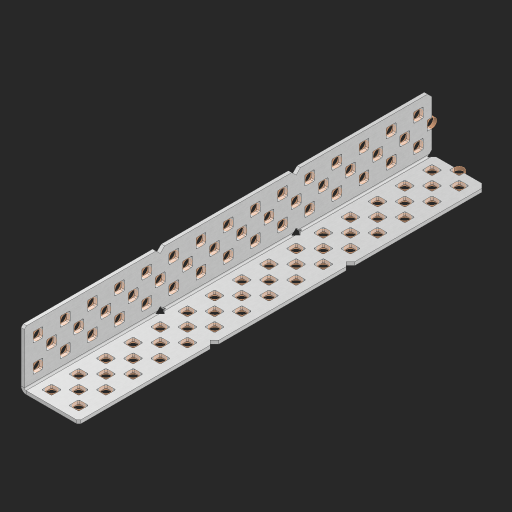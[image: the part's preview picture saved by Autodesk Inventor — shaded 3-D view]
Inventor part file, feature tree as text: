
AUTODESK INVENTOR PART (.ipt)
format: ipt  version: 2023 (Build 270158000, 158)  size: 1,245,696 bytes
history: native  units: in
note: dims shown in document units (in); Inventor stores cm internally (conversion verified against a paired STEP export)
features: other x96, extrude x88, sheet_metal_op x8, sketch x7, pattern_linear x2, mirror x1, chamfer x1
ambient origin geometry x8: Origin, YZ Plane, XZ Plane, XY Plane, X Axis, Y Axis, Z Axis, Center Point
bodies: Solid1 (feature_tree), Body (feature_tree)
feature tree (203):
  sheet_metal_op  "Flanges"
  sheet_metal_op  "Body Pattern"
  pattern_linear  "Center Pattern"  Spacing1=1.0in  [1 undecoded]
  other  "Arc Length"
  pattern_linear  "Notch Pattern"  Spacing1=0.25in  [1 undecoded]
  other  "Diagonal Plane"
  mirror  "Everything Mirrored"
  chamfer  "End Chamfer"
  sketch  "Sketch1"  dims[d0=1.0in]
  other  "Plate1"
  sketch  "Sketch2"  dims[d1=7.5in]
  other  "Plate2"
  sheet_metal_op  "Bend1"
  sheet_metal_op  "Corner1"
  sketch  "Sketch8"  dims[d2=0.0625in]
  sketch  "Sketch9"  dims[d3=0.0625in]
  other  "Srf91"
  sheet_metal_op  "Body Pattern Sketch"
  other  "Srf92"
  sketch  "Sketch13"  dims[d4=0.0312in]
  sketch  "Sketch15"  dims[d5=0.125in]
  sketch  "Sketch16"  dims[d6=0.0625in d7=1.0in d8=90.0deg d9=0.0312in d10=0.25in d11=0.0625in d12=0.0625in d49=0.182in d50=0.02in d52=0.25in d53=0.0625in d54=0.0in d55=0.172in d56=1.0in d57=0.0in d60=5.9055in d62=0.5in d63=0.7874in d65=0.5in d85=0.1473in d86=0.1782in d89=0.0625in d90=0.0in d91=0.04in d92=0.0491in d95=2.5in d96=0.04in d97=0.25in d98=45.0deg d99=0.25in d106=0.182in d107=0.02in d108=0.5in d110=0.0625in d111=0.0in d112=0.172in d113=0.5in d114=0.0in d117=0.5in d123=0.25in d125=0.25in d126=0.0491in d127=0.1473in d128=0.08in d129=0.04in d130=2.5in]
  other  "Srf786"
  other  "Srf856"
  other  "Srf857"
  other  "Srf858"
  other  "Srf859"
  other  "Srf860"
  other  "Srf861"
  other  "Srf889"
  other  "Srf890"
  other  "Srf891"
  other  "Srf1275"
  other  "Srf1276"
  other  "Srf1278"
  other  "Srf1279"
  other  "Srf1280"
  other  "Srf1281"
  other  "Srf1282"
  other  "Srf1283"
  other  "Srf1277"
  other  "Srf1285"
  other  "Srf1286"
  other  "Srf1287"
  other  "Srf1383"
  other  "Srf1384"
  other  "Srf1385"
  other  "Srf1386"
  other  "Srf1387"
  other  "Srf1388"
  other  "Srf1389"
  other  "Srf1390"
  other  "Srf1391"
  other  "Srf1392"
  other  "Srf1393"
  other  "Srf1394"
  other  "Srf1395"
  other  "Srf1396"
  other  "Srf1397"
  other  "Srf1398"
  other  "Srf1399"
  other  "Srf1400"
  other  "Srf1401"
  other  "Srf1402"
  other  "Srf1403"
  other  "Srf1404"
  other  "Srf1445"
  other  "Srf1446"
  other  "Srf1447"
  other  "Srf1448"
  other  "Srf1449"
  other  "Srf1450"
  other  "Srf1451"
  other  "Srf1452"
  other  "Srf1453"
  other  "Srf1454"
  other  "Srf1455"
  other  "Srf1475"
  other  "Srf1476"
  other  "Srf1477"
  other  "Srf1478"
  other  "Srf1479"
  other  "Srf1480"
  other  "Srf1481"
  other  "Srf1482"
  other  "Srf1483"
  other  "Srf1484"
  other  "Srf1485"
  other  "Srf1486"
  other  "Srf1487"
  other  "Srf1488"
  other  "Srf1489"
  other  "Srf1490"
  other  "Srf1491"
  other  "Srf1492"
  other  "Srf1493"
  other  "Srf1494"
  other  "Srf1495"
  other  "Srf1496"
  other  "Srf1537"
  other  "Srf1538"
  other  "Srf1539"
  other  "Srf1540"
  other  "Srf1541"
  other  "Srf1542"
  other  "Srf1543"
  other  "Srf1544"
  other  "Srf1545"
  other  "Srf1546"
  other  "Srf1547"
  sheet_metal_op  "Body Stamp"
  sheet_metal_op  "Body Circle"
  other  "Center Stamp"
  other  "Center Circle"
  sheet_metal_op  "Notch"
  extrude  "ExtrusionSrf92"  Depth=0.0625in
  extrude  "ExtrusionSrf856"  Depth=0.0625in
  extrude  "ExtrusionSrf857"  Depth=2.5in
  extrude  "ExtrusionSrf858"  Depth=2.5in
  extrude  "ExtrusionSrf859"  Depth=2.5in
  extrude  "ExtrusionSrf860"  Depth=0.0625in
  extrude  "ExtrusionSrf861"  TaperAngle=0.0deg  [1 undecoded]
  extrude  "ExtrusionSrf889"  Depth=2.5in
  extrude  "ExtrusionSrf890"  Depth=1.0in TaperAngle=0.0deg
  extrude  "ExtrusionSrf891"  Depth=2.5in
  extrude  "ExtrusionSrf1275"  Depth=0.5in
  extrude  "ExtrusionSrf1276"  Depth=2.5in
  extrude  "ExtrusionSrf1277"  Depth=2.5in
  extrude  "ExtrusionSrf1278"  Depth=0.0625in
  extrude  "ExtrusionSrf1279"  Depth=2.5in TaperAngle=0.0deg
  extrude  "ExtrusionSrf1280"  Depth=2.5in
  extrude  "ExtrusionSrf1281"  Depth=2.5in TaperAngle=45.0deg
  extrude  "ExtrusionSrf1282"  Depth=2.5in
  extrude  "ExtrusionSrf1345"  Depth=2.5in
  extrude  "ExtrusionSrf1346"  Depth=2.5in
  extrude  "ExtrusionSrf1347"  Depth=0.5in
  extrude  "ExtrusionSrf1348"  Depth=0.0625in
  extrude  "ExtrusionSrf1383"  TaperAngle=0.0deg  [1 undecoded]
  extrude  "ExtrusionSrf1384"  Depth=2.5in
  extrude  "ExtrusionSrf1385"  Depth=0.5in TaperAngle=0.0deg
  extrude  "ExtrusionSrf1386"  Depth=0.5in
  extrude  "ExtrusionSrf1387"  Depth=2.5in
  extrude  "ExtrusionSrf1388"  Depth=2.5in
  extrude  "ExtrusionSrf1389"  Depth=2.5in
  extrude  "ExtrusionSrf1390"  Depth=2.5in
  extrude  "ExtrusionSrf1391"  Depth=2.5in
  extrude  "ExtrusionSrf1392"  Depth=2.5in
  extrude  "ExtrusionSrf1393"  Depth=2.5in
  extrude  "ExtrusionSrf1394"  [1 undecoded]
  extrude  "ExtrusionSrf1395"  [1 undecoded]
  extrude  "ExtrusionSrf1396"  [1 undecoded]
  extrude  "ExtrusionSrf1397"  [1 undecoded]
  extrude  "ExtrusionSrf1398"  [1 undecoded]
  extrude  "ExtrusionSrf1399"  [1 undecoded]
  extrude  "ExtrusionSrf1400"  [1 undecoded]
  extrude  "ExtrusionSrf1401"  [1 undecoded]
  extrude  "ExtrusionSrf1402"  [1 undecoded]
  extrude  "ExtrusionSrf1403"  [1 undecoded]
  extrude  "ExtrusionSrf1404"  [1 undecoded]
  extrude  "ExtrusionSrf1445"  [1 undecoded]
  extrude  "ExtrusionSrf1446"  [1 undecoded]
  extrude  "ExtrusionSrf1447"  [1 undecoded]
  extrude  "ExtrusionSrf1448"  [1 undecoded]
  extrude  "ExtrusionSrf1449"  [1 undecoded]
  extrude  "ExtrusionSrf1450"  [1 undecoded]
  extrude  "ExtrusionSrf1451"  [1 undecoded]
  extrude  "ExtrusionSrf1452"  [1 undecoded]
  extrude  "ExtrusionSrf1453"  [1 undecoded]
  extrude  "ExtrusionSrf1454"  [1 undecoded]
  extrude  "ExtrusionSrf1455"  [1 undecoded]
  extrude  "ExtrusionSrf1475"  [1 undecoded]
  extrude  "ExtrusionSrf1476"  [1 undecoded]
  extrude  "ExtrusionSrf1477"  [1 undecoded]
  extrude  "ExtrusionSrf1478"  [1 undecoded]
  extrude  "ExtrusionSrf1479"  [1 undecoded]
  extrude  "ExtrusionSrf1480"  [1 undecoded]
  extrude  "ExtrusionSrf1481"  [1 undecoded]
  extrude  "ExtrusionSrf1482"  [1 undecoded]
  extrude  "ExtrusionSrf1483"  [1 undecoded]
  extrude  "ExtrusionSrf1484"  [1 undecoded]
  extrude  "ExtrusionSrf1485"  [1 undecoded]
  extrude  "ExtrusionSrf1486"  [1 undecoded]
  extrude  "ExtrusionSrf1487"  [1 undecoded]
  extrude  "ExtrusionSrf1488"  [1 undecoded]
  extrude  "ExtrusionSrf1489"  [1 undecoded]
  extrude  "ExtrusionSrf1490"  [1 undecoded]
  extrude  "ExtrusionSrf1491"  [1 undecoded]
  extrude  "ExtrusionSrf1492"  [1 undecoded]
  extrude  "ExtrusionSrf1493"  [1 undecoded]
  extrude  "ExtrusionSrf1494"  [1 undecoded]
  extrude  "ExtrusionSrf1495"  [1 undecoded]
  extrude  "ExtrusionSrf1496"  [1 undecoded]
  extrude  "ExtrusionSrf1537"  [1 undecoded]
  extrude  "ExtrusionSrf1538"  [1 undecoded]
  extrude  "ExtrusionSrf1539"  [1 undecoded]
  extrude  "ExtrusionSrf1540"  [1 undecoded]
  extrude  "ExtrusionSrf1541"  [1 undecoded]
  extrude  "ExtrusionSrf1542"  [1 undecoded]
  extrude  "ExtrusionSrf1543"  [1 undecoded]
  extrude  "ExtrusionSrf1544"  [1 undecoded]
  extrude  "ExtrusionSrf1545"  [1 undecoded]
  extrude  "ExtrusionSrf1546"  [1 undecoded]
  extrude  "ExtrusionSrf1547"  [1 undecoded]
note: 59 required parameter values undecoded (feature->parameter linkage not recoverable at this tier; creation-order binding heuristic only, values carry confidence <= 0.55)
